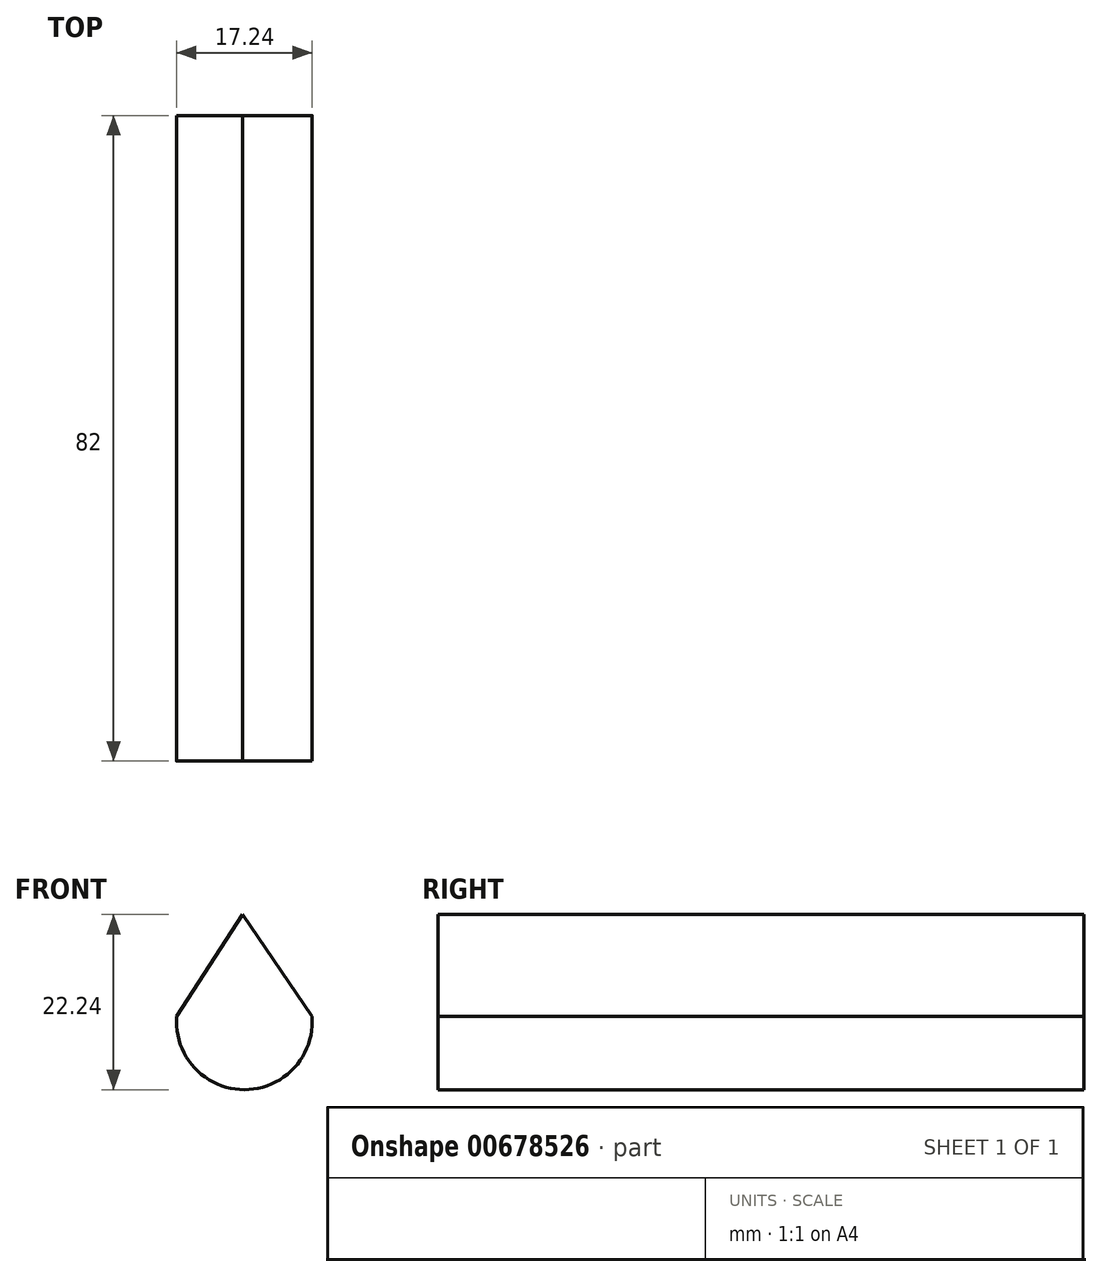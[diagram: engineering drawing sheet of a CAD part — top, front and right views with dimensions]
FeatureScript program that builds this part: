
annotation { "Feature Type Name" : "Feature", "Feature Type Description" : "" }
export const myFeature = defineFeature(function(context is Context, id is Id, definition is map)
    precondition{}
    {
        {
            var Q0;
            Q0=qCreatedBy(makeId("Front.planeOp"),FACE);
            var sketch = newSketch(context, id + "F0", { "sketchPlane" : qUnion([Q0])});
            skLineSegment(sketch, "E0", {"start": v(-9.8, -1.06) * mm, "end": v(-1.44, 11.89) * mm});
            skLineSegment(sketch, "E1", {"start": v(-1.44, 11.89) * mm, "end": v(7.37, -1.06) * mm});
            skArc(sketch, "E2", {"start": v(-9.8, -1.06) * mm, "mid": v(-1.22, -10.35) * mm, "end": v(7.37, -1.06) * mm});
            skSolve(sketch);
        }
        {
            var Q0;
            Q0=makeQuery(id+"F0.imprint","IMPRINT",FACE,{"disambiguationData":[TD([[makeQuery(id+"F0.imprint","IMPRINT",EDGE,{"derivedFrom":sQuery(id+"F0.wireOp",EDGE,"E0")}),-1.0]])]});
            extrude(context, id + "F1", {"entities" : qUnion([Q0]), "depth" : 82 * mm, "offsetDistance" : 25 * mm});
        }
    });
